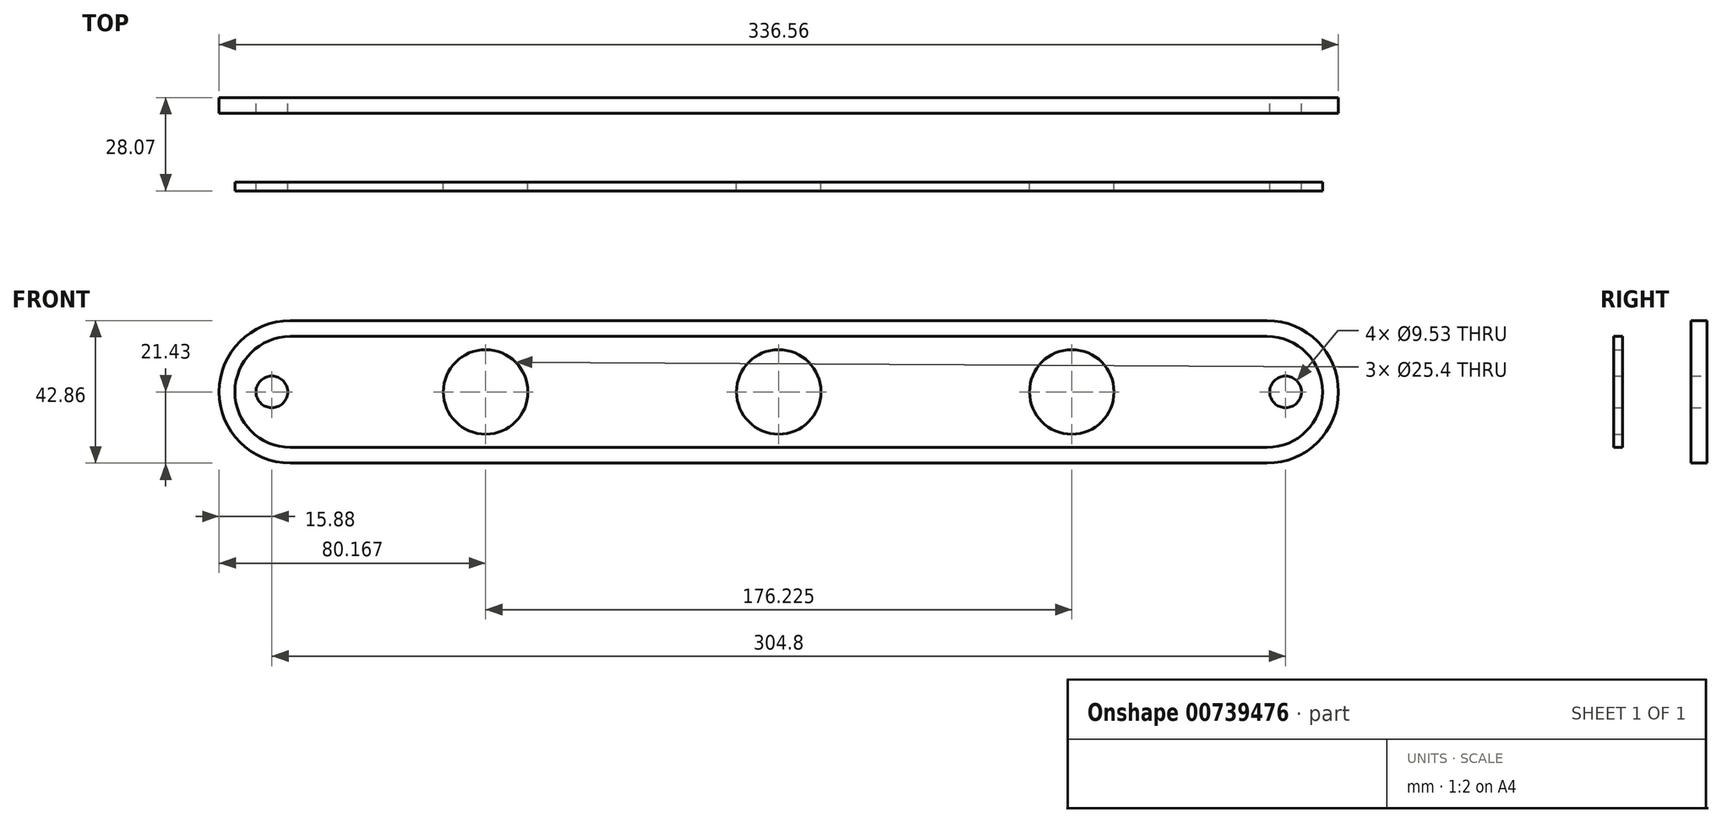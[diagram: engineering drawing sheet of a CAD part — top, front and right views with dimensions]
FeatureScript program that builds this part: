
annotation { "Feature Type Name" : "Feature", "Feature Type Description" : "" }
export const myFeature = defineFeature(function(context is Context, id is Id, definition is map)
    precondition{}
    {
        {
            var Q0;
            Q0=qCreatedBy(makeId("Front.planeOp"),FACE);
            var sketch = newSketch(context, id + "F0", { "sketchPlane" : qUnion([Q0])});
            skLineSegment(sketch, "E0.bottom", {"start": v(146.84, 21.43) * mm, "end": v(-146.84, 21.43) * mm});
            skLineSegment(sketch, "E0.top", {"start": v(146.84, -21.43) * mm, "end": v(-146.84, -21.43) * mm});
            skPoint(sketch, "E0.middle", {"position": v(0, 0) * mm});
            skArc(sketch, "E1", {"start": v(-146.84, 21.43) * mm, "mid": v(-168.27, 0) * mm, "end": v(-146.84, -21.43) * mm});
            skArc(sketch, "E2", {"start": v(146.84, -21.43) * mm, "mid": v(168.28, 0) * mm, "end": v(146.84, 21.43) * mm});
            skLineSegment(sketch, "E3", {"start": v(186.76, 0) * mm, "end": v(-183.78, 0) * mm, "construction": true});
            skPoint(sketch, "E3.endSnap0", {"position": v(-168.27, 0) * mm});
            skCircle(sketch, "E4", {"center": v(-152.4, 0) * mm, "radius": 4.76 * mm});
            skCircle(sketch, "E5", {"center": v(152.4, 0) * mm, "radius": 4.76 * mm});
            skPoint(sketch, "E6", {"position": v(168.28, 0) * mm});
            skSolve(sketch);
        }
        {
            var Q0;
            Q0=makeQuery(id+"F0.imprint","IMPRINT",FACE,{"disambiguationData":[TD([[makeQuery(id+"F0.imprint","IMPRINT",EDGE,{"derivedFrom":sQuery(id+"F0.wireOp",EDGE,"E0.bottom")}),1.0]])]});
            extrude(context, id + "F1", {"entities" : qUnion([Q0]), "depth" : 4.75 * mm, "offsetDistance" : 25.4 * mm});
        }
        {
            var Q0;
            Q0=qCreatedBy(makeId("Front.planeOp"),FACE);
            cPlane(context, id + "F2", {"entities" : qUnion([Q0]), "cplaneType" : CPlaneType.OFFSET, "offset" : 25.4 * mm, "width" : 152.4 * mm, "height" : 152.4 * mm});
        }
        {
            var Q0;
            Q0=qCreatedBy(id+"F2.planeOp",FACE);
            var sketch = newSketch(context, id + "F3", { "sketchPlane" : qUnion([Q0])});
            skCircle(sketch, "E7.0", {"center": v(-152.4, 0) * mm, "radius": 4.76 * mm});
            skCircle(sketch, "E8.0", {"center": v(152.4, 0) * mm, "radius": 4.76 * mm});
            skLineSegment(sketch, "E9.0", {"start": v(146.84, 21.43) * mm, "end": v(-146.84, 21.43) * mm});
            skArc(sketch, "E10.0", {"start": v(-146.84, 21.43) * mm, "mid": v(-168.28, 0) * mm, "end": v(-146.84, -21.43) * mm});
            skLineSegment(sketch, "E11.0", {"start": v(146.84, -21.43) * mm, "end": v(-146.84, -21.43) * mm});
            skArc(sketch, "E12.0", {"start": v(146.84, -21.43) * mm, "mid": v(168.28, 0) * mm, "end": v(146.84, 21.43) * mm});
            skLineSegment(sketch, "E13.0", {"start": v(146.84, 16.68) * mm, "end": v(-146.84, 16.68) * mm});
            skArc(sketch, "E13.1", {"start": v(146.84, -16.68) * mm, "mid": v(163.53, 0) * mm, "end": v(146.84, 16.68) * mm});
            skLineSegment(sketch, "E13.2", {"start": v(146.84, -16.68) * mm, "end": v(-146.84, -16.68) * mm});
            skArc(sketch, "E13.3", {"start": v(-146.84, 16.68) * mm, "mid": v(-163.53, 0) * mm, "end": v(-146.84, -16.68) * mm});
            skLineSegment(sketch, "E14", {"start": v(-189.54, 0) * mm, "end": v(192.95, 0) * mm, "construction": true});
            skCircle(sketch, "E15", {"center": v(-88.11, 0) * mm, "radius": 12.7 * mm});
            skCircle(sketch, "E16", {"center": v(0, 0) * mm, "radius": 12.7 * mm});
            skCircle(sketch, "E17", {"center": v(88.11, 0) * mm, "radius": 12.7 * mm});
            skSolve(sketch);
        }
        {
            var Q0;
            Q0=makeQuery(id+"F3.imprint","IMPRINT",FACE,{"disambiguationData":[TD([[makeQuery(id+"F3.imprint","IMPRINT",EDGE,{"derivedFrom":sQuery(id+"F3.wireOp",EDGE,"E7.0")}),-1.0]])]});
            extrude(context, id + "F4", {"entities" : qUnion([Q0]), "depth" : 2.67 * mm, "offsetDistance" : 25.4 * mm});
        }
    });
